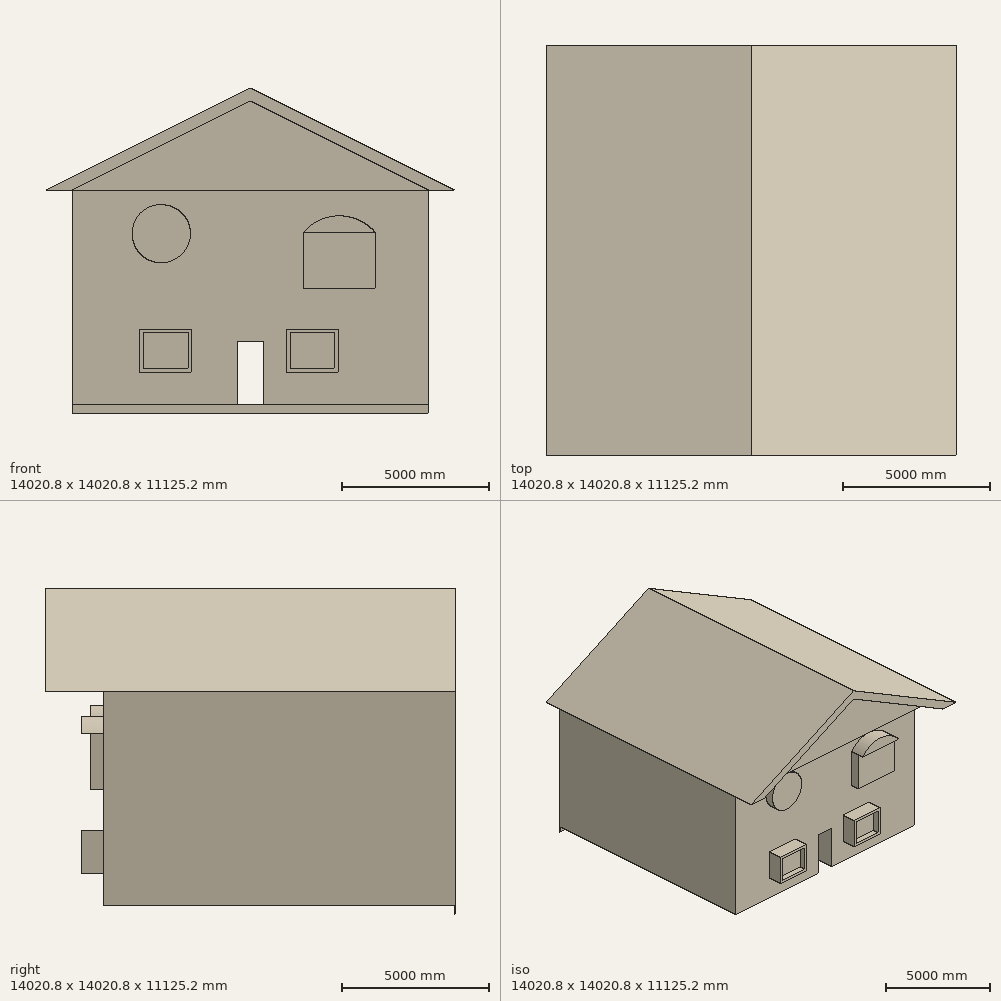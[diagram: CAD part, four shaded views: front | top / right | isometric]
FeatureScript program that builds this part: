
annotation { "Feature Type Name" : "Feature", "Feature Type Description" : "" }
export const myFeature = defineFeature(function(context is Context, id is Id, definition is map)
    precondition{}
    {
        {
            var Q0;
            Q0=qCreatedBy(makeId("Front.planeOp"),FACE);
            var sketch = newSketch(context, id + "F0", { "sketchPlane" : qUnion([Q0])});
            skLineSegment(sketch, "E0", {"start": v(0, 0) * mm, "end": v(-6096, 0) * mm});
            skLineSegment(sketch, "E1", {"start": v(0, 0) * mm, "end": v(6096, 0) * mm});
            skLineSegment(sketch, "E2", {"start": v(0, 0) * mm, "end": v(0, 3048) * mm, "construction": true});
            skLineSegment(sketch, "E3", {"start": v(0, 3048) * mm, "end": v(-6096, 0) * mm});
            skLineSegment(sketch, "E4", {"start": v(0, 3048) * mm, "end": v(6096, 0) * mm});
            skLineSegment(sketch, "E5", {"start": v(6096, 0) * mm, "end": v(7010.4, 0) * mm});
            skLineSegment(sketch, "E6", {"start": v(-6096, 0) * mm, "end": v(-7010.4, 0) * mm});
            skLineSegment(sketch, "E7", {"start": v(0, 3048) * mm, "end": v(0, 3505.2) * mm});
            skLineSegment(sketch, "E8", {"start": v(0, 3505.2) * mm, "end": v(7010.4, 0) * mm});
            skLineSegment(sketch, "E9", {"start": v(0, 3505.2) * mm, "end": v(-7010.4, 0) * mm});
            skLineSegment(sketch, "E10", {"start": v(-6096, 0) * mm, "end": v(-6096, -7315.2) * mm});
            skLineSegment(sketch, "E11", {"start": v(-6096, -7315.2) * mm, "end": v(6096, -7315.2) * mm});
            skLineSegment(sketch, "E12", {"start": v(6096, 0) * mm, "end": v(6096, -7315.2) * mm});
            skLineSegment(sketch, "E13", {"start": v(-6096, -7315.2) * mm, "end": v(-6096, -7620) * mm});
            skLineSegment(sketch, "E14", {"start": v(6096, -7315.2) * mm, "end": v(6096, -7620) * mm});
            skLineSegment(sketch, "E15", {"start": v(6096, -7620) * mm, "end": v(-6096, -7620) * mm});
            skLineSegment(sketch, "E16", {"start": v(0, -7315.2) * mm, "end": v(-457.2, -7315.2) * mm});
            skLineSegment(sketch, "E17", {"start": v(0, -7315.2) * mm, "end": v(457.2, -7315.2) * mm});
            skLineSegment(sketch, "E18", {"start": v(-457.2, -7315.2) * mm, "end": v(-457.2, -5181.6) * mm});
            skLineSegment(sketch, "E19", {"start": v(-457.2, -5181.6) * mm, "end": v(0, -5181.6) * mm});
            skLineSegment(sketch, "E20", {"start": v(0, -5181.6) * mm, "end": v(457.2, -5181.6) * mm});
            skLineSegment(sketch, "E21", {"start": v(457.2, -5181.6) * mm, "end": v(457.2, -7315.2) * mm});
            skLineSegment(sketch, "E22.bottom", {"start": v(-3657.6, -4876.8) * mm, "end": v(-2133.6, -4876.8) * mm});
            skLineSegment(sketch, "E22.top", {"start": v(-3657.6, -6096) * mm, "end": v(-2133.6, -6096) * mm});
            skLineSegment(sketch, "E22.left", {"start": v(-3657.6, -4876.8) * mm, "end": v(-3657.6, -6096) * mm});
            skLineSegment(sketch, "E22.right", {"start": v(-2133.6, -4876.8) * mm, "end": v(-2133.6, -6096) * mm});
            skLineSegment(sketch, "E23.0", {"start": v(-3779.52, -4754.88) * mm, "end": v(-2011.68, -4754.88) * mm});
            skLineSegment(sketch, "E23.1", {"start": v(-3779.52, -4754.88) * mm, "end": v(-3779.52, -6217.92) * mm});
            skLineSegment(sketch, "E23.2", {"start": v(-3779.52, -6217.92) * mm, "end": v(-2011.68, -6217.92) * mm});
            skLineSegment(sketch, "E23.3", {"start": v(-2011.68, -4754.88) * mm, "end": v(-2011.68, -6217.92) * mm});
            skLineSegment(sketch, "E24.bottom", {"start": v(2880.3, -4876.8) * mm, "end": v(1356.3, -4876.8) * mm});
            skLineSegment(sketch, "E24.top", {"start": v(2880.3, -6096) * mm, "end": v(1356.3, -6096) * mm});
            skLineSegment(sketch, "E24.left", {"start": v(2880.3, -4876.8) * mm, "end": v(2880.3, -6096) * mm});
            skLineSegment(sketch, "E24.right", {"start": v(1356.3, -4876.8) * mm, "end": v(1356.3, -6096) * mm});
            skLineSegment(sketch, "E25.0", {"start": v(3002.22, -4754.88) * mm, "end": v(1234.38, -4754.88) * mm});
            skLineSegment(sketch, "E25.1", {"start": v(3002.22, -4754.88) * mm, "end": v(3002.22, -6217.92) * mm});
            skLineSegment(sketch, "E25.2", {"start": v(3002.22, -6217.92) * mm, "end": v(1234.38, -6217.92) * mm});
            skLineSegment(sketch, "E25.3", {"start": v(1234.38, -4754.88) * mm, "end": v(1234.38, -6217.92) * mm});
            skCircle(sketch, "E26", {"center": v(-3048, -1485.09) * mm, "radius": 996.6 * mm});
            skLineSegment(sketch, "E27.bottom", {"start": v(1828.8, -1439.86) * mm, "end": v(4267.2, -1439.86) * mm});
            skLineSegment(sketch, "E27.top", {"start": v(1828.8, -3352.8) * mm, "end": v(4267.2, -3352.8) * mm});
            skLineSegment(sketch, "E27.left", {"start": v(1828.8, -1439.86) * mm, "end": v(1828.8, -3352.8) * mm});
            skLineSegment(sketch, "E27.right", {"start": v(4267.2, -1439.86) * mm, "end": v(4267.2, -3352.8) * mm});
            skArc(sketch, "E28", {"start": v(4267.2, -1439.86) * mm, "mid": v(3048, -871.06) * mm, "end": v(1828.8, -1439.86) * mm});
            skSolve(sketch);
        }
        {
            var Q0;
            Q0=makeQuery(id+"F0.imprint","IMPRINT",FACE,{"disambiguationData":[TD([[makeQuery(id+"F0.imprint","IMPRINT",EDGE,{"derivedFrom":sQuery(id+"F0.wireOp",EDGE,"E3")}),-1.0]])]});
            var Q1;
            Q1=makeQuery(id+"F0.imprint","IMPRINT",FACE,{"disambiguationData":[TD([[makeQuery(id+"F0.imprint","IMPRINT",EDGE,{"derivedFrom":sQuery(id+"F0.wireOp",EDGE,"E4")}),1.0]])]});
            extrude(context, id + "F1", {"entities" : qUnion([Q0, Q1]), "depth" : 14020.8 * mm, "offsetDistance" : 30.48 * mm});
        }
        {
            var Q0;
            Q0=makeQuery(id+"F0.imprint","IMPRINT",FACE,{"disambiguationData":[TD([[makeQuery(id+"F0.imprint","IMPRINT",EDGE,{"derivedFrom":sQuery(id+"F0.wireOp",EDGE,"E0")}),-1.0]])]});
            extrude(context, id + "F2", {"entities" : qUnion([Q0]), "operationType" : NewBodyOperationType.ADD, "depth" : 13106.4 * mm, "offsetDistance" : 30.48 * mm});
        }
        {
            var Q0;
            Q0=makeQuery(id+"F0.imprint","IMPRINT",FACE,{"disambiguationData":[TD([[makeQuery(id+"F0.imprint","IMPRINT",EDGE,{"derivedFrom":sQuery(id+"F0.wireOp",EDGE,"E4")}),1.0]])]});
            var Q1;
            Q1=makeQuery(id+"F0.imprint","IMPRINT",FACE,{"disambiguationData":[TD([[makeQuery(id+"F0.imprint","IMPRINT",EDGE,{"derivedFrom":sQuery(id+"F0.wireOp",EDGE,"E3")}),-1.0]])]});
            extrude(context, id + "F3", {"entities" : qUnion([Q0, Q1]), "depth" : 914.4 * mm, "offsetDistance" : 30.48 * mm});
        }
        {
            var Q0;
            Q0=makeQuery(id+"F0.imprint","IMPRINT",FACE,{"disambiguationData":[TD([[makeQuery(id+"F0.imprint","IMPRINT",EDGE,{"derivedFrom":sQuery(id+"F0.wireOp",EDGE,"E0")}),1.0]])]});
            extrude(context, id + "F4", {"entities" : qUnion([Q0]), "operationType" : NewBodyOperationType.ADD, "depth" : 12039.6 * mm, "offsetDistance" : 30.48 * mm});
        }
        {
            var Q0;
            Q0=makeQuery(id+"F0.imprint","IMPRINT",FACE,{"disambiguationData":[TD([[makeQuery(id+"F0.imprint","IMPRINT",EDGE,{"derivedFrom":sQuery(id+"F0.wireOp",EDGE,"E27.bottom")}),1.0]])]});
            var Q1;
            Q1=makeQuery(id+"F0.imprint","IMPRINT",FACE,{"disambiguationData":[TD([[makeQuery(id+"F0.imprint","IMPRINT",EDGE,{"derivedFrom":sQuery(id+"F0.wireOp",EDGE,"E24.bottom")}),-1.0]])]});
            var Q2;
            Q2=makeQuery(id+"F0.imprint","IMPRINT",FACE,{"disambiguationData":[TD([[makeQuery(id+"F0.imprint","IMPRINT",EDGE,{"derivedFrom":sQuery(id+"F0.wireOp",EDGE,"E22.bottom")}),1.0]])]});
            extrude(context, id + "F5", {"entities" : qUnion([Q0, Q1, Q2]), "operationType" : NewBodyOperationType.ADD, "depth" : 12801.6 * mm, "offsetDistance" : 30.48 * mm});
        }
        {
            var Q0;
            Q0=makeQuery(id+"F0.imprint","IMPRINT",FACE,{"disambiguationData":[TD([[makeQuery(id+"F0.imprint","IMPRINT",EDGE,{"derivedFrom":sQuery(id+"F0.wireOp",EDGE,"E27.bottom")}),-1.0]])]});
            var Q1;
            Q1=makeQuery(id+"F0.imprint","IMPRINT",FACE,{"disambiguationData":[TD([[makeQuery(id+"F0.imprint","IMPRINT",EDGE,{"derivedFrom":sQuery(id+"F0.wireOp",EDGE,"E26")}),1.0]])]});
            var Q2;
            Q2=makeQuery(id+"F0.imprint","IMPRINT",FACE,{"disambiguationData":[TD([[makeQuery(id+"F0.imprint","IMPRINT",EDGE,{"derivedFrom":sQuery(id+"F0.wireOp",EDGE,"E22.bottom")}),-1.0]])]});
            var Q3;
            Q3=makeQuery(id+"F0.imprint","IMPRINT",FACE,{"disambiguationData":[TD([[makeQuery(id+"F0.imprint","IMPRINT",EDGE,{"derivedFrom":sQuery(id+"F0.wireOp",EDGE,"E16")}),-1.0]])]});
            var Q4;
            Q4=makeQuery(id+"F0.imprint","IMPRINT",FACE,{"disambiguationData":[TD([[makeQuery(id+"F0.imprint","IMPRINT",EDGE,{"derivedFrom":sQuery(id+"F0.wireOp",EDGE,"E24.bottom")}),1.0]])]});
            extrude(context, id + "F6", {"entities" : qUnion([Q0, Q1, Q2, Q3, Q4]), "operationType" : NewBodyOperationType.ADD, "depth" : 12496.8 * mm, "offsetDistance" : 30.48 * mm});
        }
        {
            var Q0;
            {var subQ1=sQuery(id+"F0.wireOp",EDGE,"E13");Q0=makeQuery(id+"F0.imprint","IMPRINT",FACE,{"disambiguationData":[TD([[makeQuery(id+"F0.imprint","IMPRINT",EDGE,{"derivedFrom":subQ1}),1.0]])]});}
            extrude(context, id + "F7", {"entities" : qUnion([Q0]), "operationType" : NewBodyOperationType.ADD, "depth" : 30.48 * mm, "offsetDistance" : 30.48 * mm});
        }
    });
